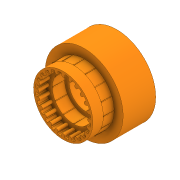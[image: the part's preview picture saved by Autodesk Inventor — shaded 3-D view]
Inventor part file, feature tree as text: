
AUTODESK INVENTOR PART (.ipt)
format: ipt  version: 2020 (Build 240168000, 168)  size: 561,152 bytes
history: native  units: in
note: dims shown in document units (in); Inventor stores cm internally (conversion verified against a paired STEP export)
features: extrude x6, sketch x6, chamfer x2, projected_geometry x1
ambient origin geometry x8: Origin, YZ Plane, XZ Plane, XY Plane, X Axis, Y Axis, Z Axis, Center Point
bodies: Solid1 (feature_tree)
feature tree (15):
  extrude  "Extrusion1"  Depth=2.0472in
  extrude  "Extrusion2"  Depth=1.1024in
  chamfer  "Chamfer2"  Distance=0.2756in
  extrude  "Extrusion4"  Depth=0.0157in
  extrude  "Extrusion5"  Depth=0.2756in TaperAngle=0.0deg
  extrude  "Extrusion7"  Depth=0.0394in
  chamfer  "Chamfer4"  Distance=1.4567in
  extrude  "Extrusion8"  Depth=0.042in
  sketch  "Sketch1"  dims[d0=0.8661in d1=2.0472in]
  sketch  "Sketch2"  dims[d2=0.8563in d3=0.0in d4=1.1024in]
  sketch  "Sketch4"  dims[d5=1.5748in d6=0.2756in d7=0.0in]
  sketch  "Sketch5"  dims[d11=0.2756in d12=0.125in d13=0.0137in d25=0.0157in]
  sketch  "Sketch8"  dims[d26=6.2992in d28=360.0deg d30=0.2756in d31=0.0in]
  projected_geometry  "Projected Loop2"
  sketch  "Sketch10"  dims[d33=0.0394in d38=0.0394in d39=1.4567in d40=0.042in d41=0.042in d42=0.042in d43=9.4488in d45=360.0deg d47=0.2756in d48=0.0in d49=1.2598in d57=0.0394in d58=0.0in d59=0.315in d60=0.125in d61=0.0137in d67=0.0157in d68=4.7244in d70=360.0deg d72=0.0394in d73=0.0in]
